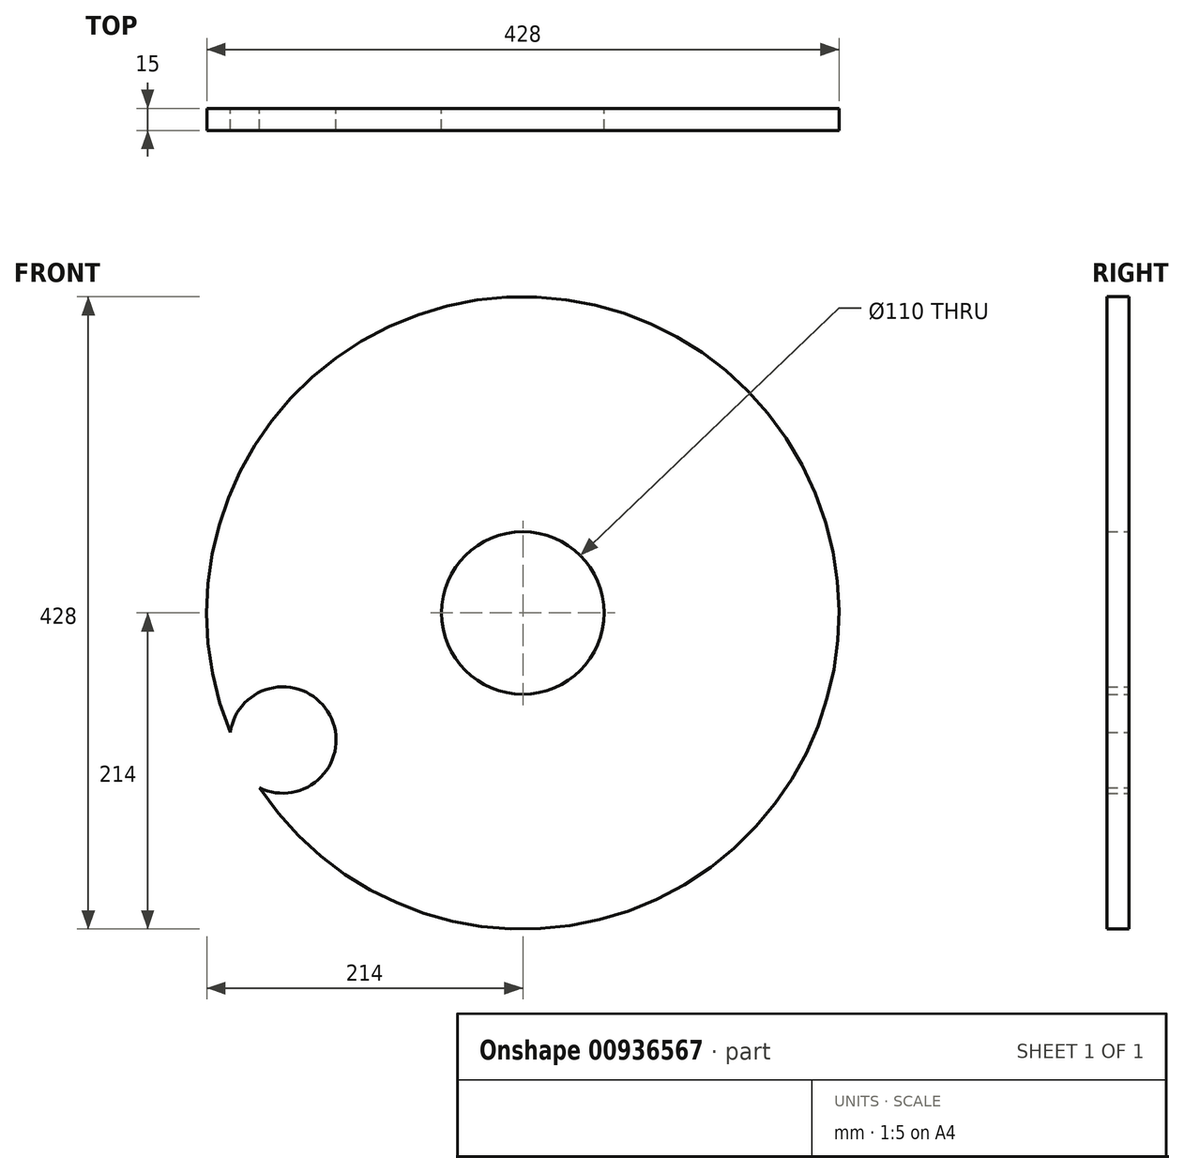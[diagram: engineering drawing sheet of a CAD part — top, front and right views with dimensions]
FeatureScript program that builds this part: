
annotation { "Feature Type Name" : "Feature", "Feature Type Description" : "" }
export const myFeature = defineFeature(function(context is Context, id is Id, definition is map)
    precondition{}
    {
        {
            var Q0;
            Q0=qCreatedBy(makeId("Front.planeOp"),FACE);
            var sketch = newSketch(context, id + "F0", { "sketchPlane" : qUnion([Q0])});
            skCircle(sketch, "E0", {"center": v(0, 0) * mm, "radius": 214 * mm});
            skCircle(sketch, "E1", {"center": v(0, 0) * mm, "radius": 55 * mm});
            skCircle(sketch, "E2", {"center": v(-162.47, -86.03) * mm, "radius": 36 * mm});
            skLineSegment(sketch, "E3", {"start": v(0, 0) * mm, "end": v(0, 106.67) * mm});
            skLineSegment(sketch, "E4", {"start": v(-214, 0) * mm, "end": v(-214, 117.68) * mm});
            skLineSegment(sketch, "E5", {"start": v(-152, 0) * mm, "end": v(-152, 117) * mm});
            skSolve(sketch);
        }
        {
            var Q0;
            Q0=makeQuery(id+"F0.imprint","IMPRINT",FACE,{"disambiguationData":[TD([[makeQuery(id+"F0.imprint","IMPRINT",EDGE,{"derivedFrom":sQuery(id+"F0.wireOp",EDGE,"E0")}),1.0]])]});
            extrude(context, id + "F1", {"entities" : qUnion([Q0]), "depth" : 15 * mm, "offsetDistance" : 25 * mm});
        }
    });
